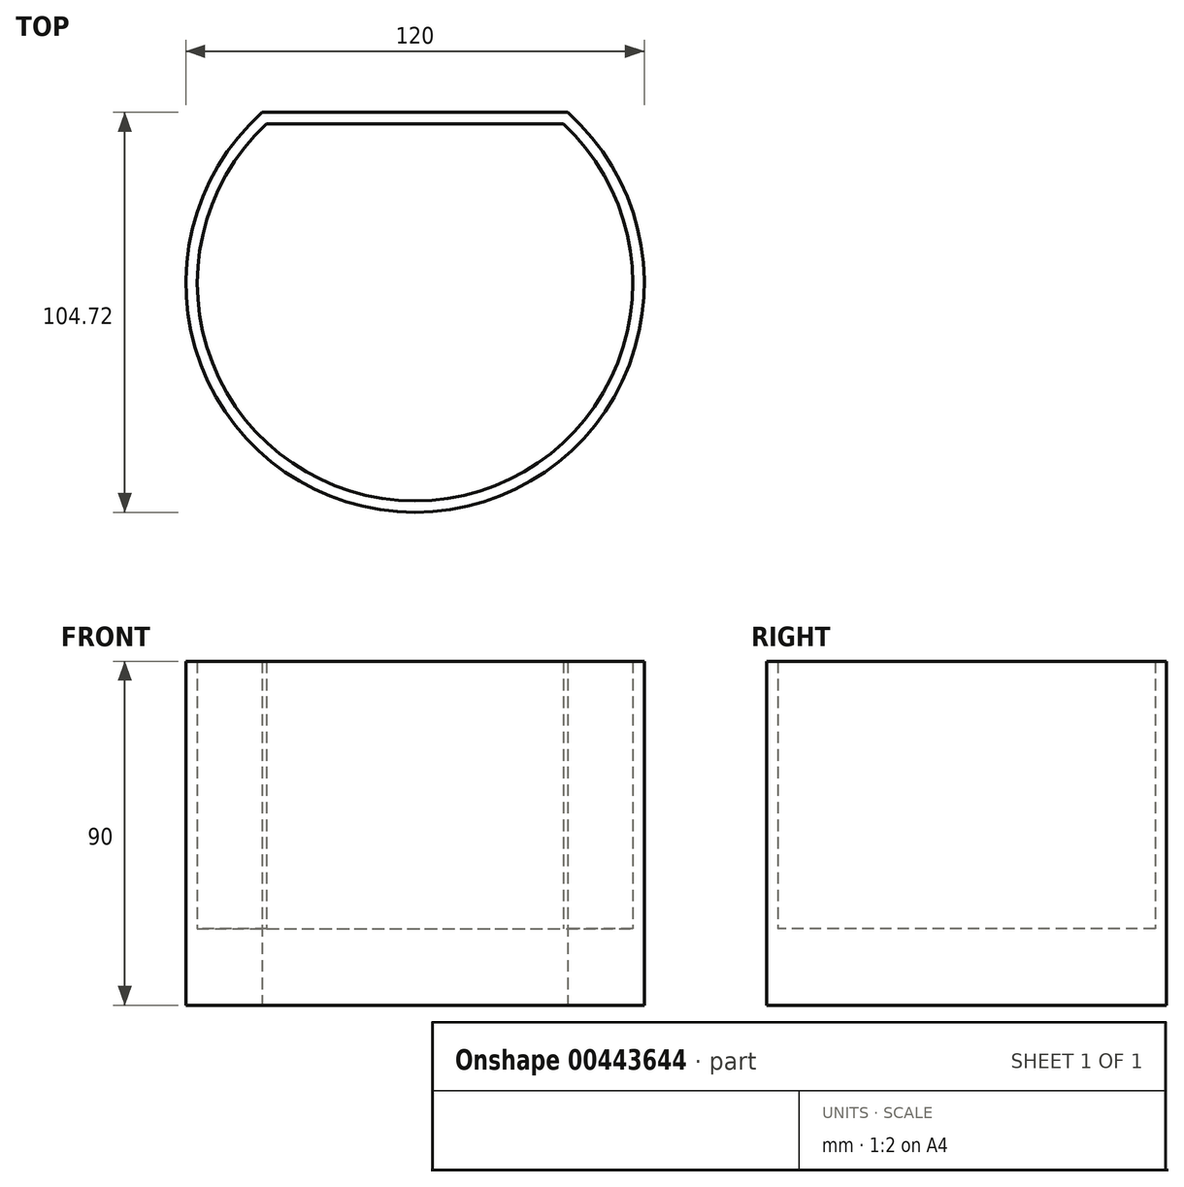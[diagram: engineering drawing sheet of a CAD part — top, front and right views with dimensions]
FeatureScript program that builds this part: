
annotation { "Feature Type Name" : "Feature", "Feature Type Description" : "" }
export const myFeature = defineFeature(function(context is Context, id is Id, definition is map)
    precondition{}
    {
        {
            var Q0;
            Q0=qCreatedBy(makeId("Top.planeOp"),FACE);
            var sketch = newSketch(context, id + "F0", { "sketchPlane" : qUnion([Q0])});
            skArc(sketch, "E0", {"start": v(-40, 44.72) * mm, "mid": v(0, -60) * mm, "end": v(40, 44.72) * mm});
            skLineSegment(sketch, "E1", {"start": v(-40, 44.72) * mm, "end": v(40, 44.72) * mm});
            skSolve(sketch);
        }
        {
            var Q0;
            Q0=makeQuery(id+"F0.imprint","IMPRINT",FACE,{"disambiguationData":[TD([[makeQuery(id+"F0.imprint","IMPRINT",EDGE,{"derivedFrom":sQuery(id+"F0.wireOp",EDGE,"E0")}),1.0]])]});
            extrude(context, id + "F1", {"entities" : qUnion([Q0]), "depth" : 20 * mm});
        }
        {
            var Q0;
            Q0=makeQuery(id+"F1.opExtrude","CAP_FACE",FACE,{"disambiguationData":[OSD([sQuery(id+"F0.wireOp",EDGE,"E0"),sQuery(id+"F0.wireOp",EDGE,"E1")])],"isStart":false});
            var sketch = newSketch(context, id + "F2", { "sketchPlane" : qUnion([Q0])});
            skArc(sketch, "E2", {"start": v(-40, 44.72) * mm, "mid": v(0, -60) * mm, "end": v(40, 44.72) * mm});
            skLineSegment(sketch, "E3", {"start": v(-40, 44.72) * mm, "end": v(40, 44.72) * mm});
            skArc(sketch, "E4", {"start": v(-38.84, 41.72) * mm, "mid": v(0, -57) * mm, "end": v(38.84, 41.72) * mm});
            skLineSegment(sketch, "E5", {"start": v(-38.84, 41.72) * mm, "end": v(38.84, 41.72) * mm});
            skSolve(sketch);
        }
        {
            var Q0;
            Q0=makeQuery(id+"F2.imprint","IMPRINT",FACE,{"disambiguationData":[TD([[makeQuery(id+"F2.imprint","IMPRINT",EDGE,{"derivedFrom":sQuery(id+"F2.wireOp",EDGE,"E2")}),1.0]])]});
            extrude(context, id + "F3", {"entities" : qUnion([Q0]), "operationType" : NewBodyOperationType.ADD, "depth" : 70 * mm});
        }
    });
